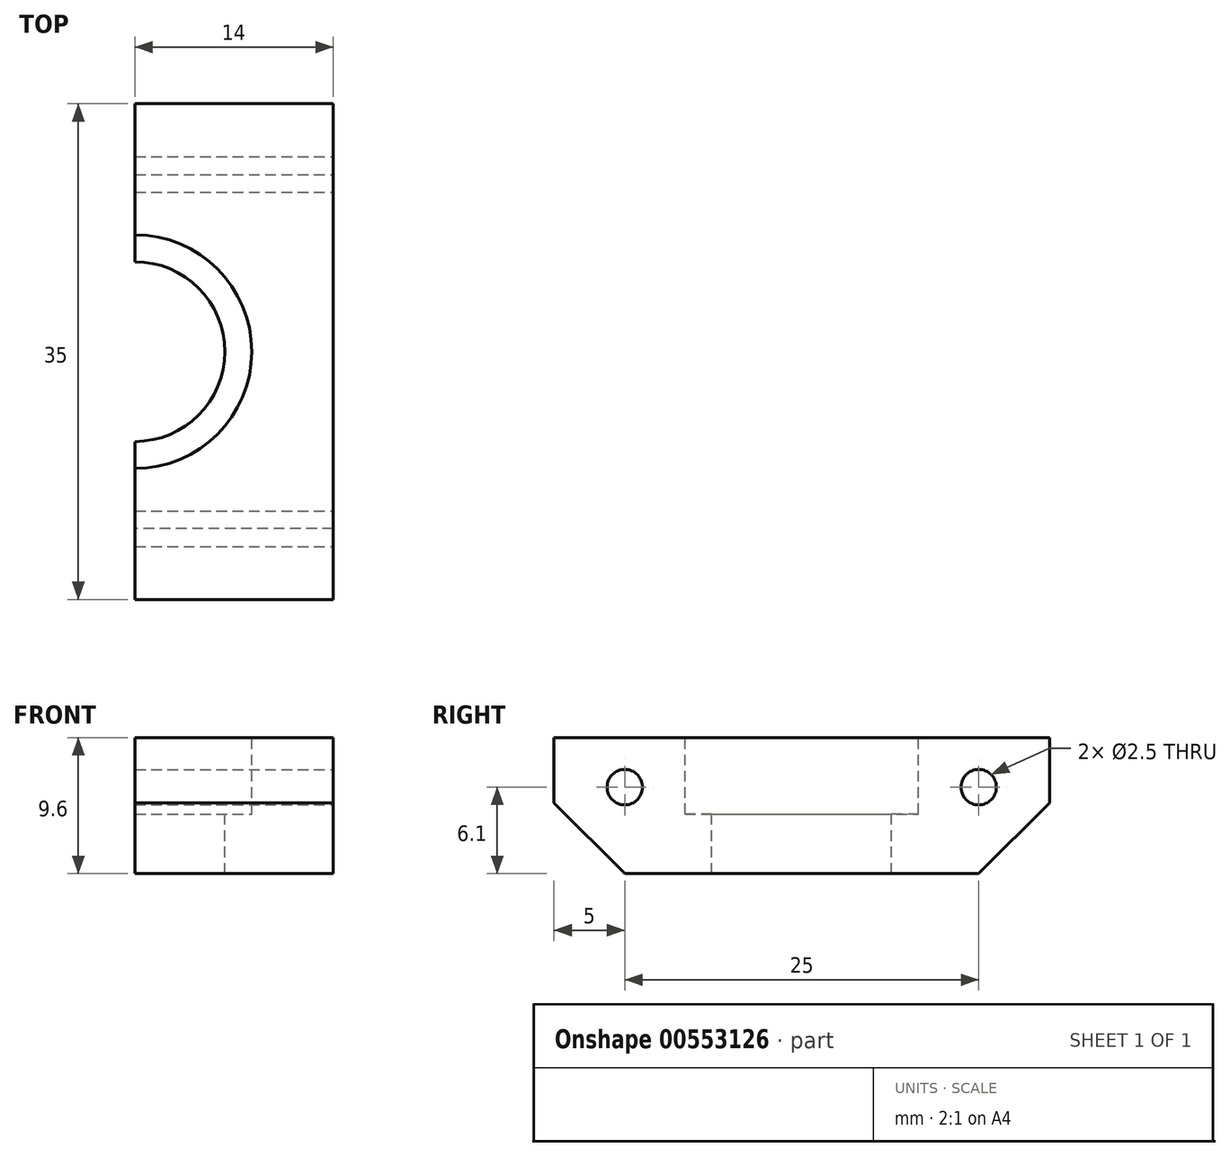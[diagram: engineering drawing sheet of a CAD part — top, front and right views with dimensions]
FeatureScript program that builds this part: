
annotation { "Feature Type Name" : "Feature", "Feature Type Description" : "" }
export const myFeature = defineFeature(function(context is Context, id is Id, definition is map)
    precondition{}
    {
        {
            var Q0;
            Q0=qCreatedBy(makeId("Right.planeOp"),FACE);
            var sketch = newSketch(context, id + "F0", { "sketchPlane" : qUnion([Q0])});
            skLineSegment(sketch, "E0.bottom", {"start": v(-17.5, -4.8) * mm, "end": v(17.5, -4.8) * mm});
            skLineSegment(sketch, "E0.top", {"start": v(-17.5, 4.8) * mm, "end": v(17.5, 4.8) * mm});
            skLineSegment(sketch, "E0.left", {"start": v(-17.5, -4.8) * mm, "end": v(-17.5, 4.8) * mm});
            skLineSegment(sketch, "E0.right", {"start": v(17.5, -4.8) * mm, "end": v(17.5, 4.8) * mm});
            skPoint(sketch, "E0.middle", {"position": v(0, 0) * mm});
            skSolve(sketch);
        }
        {
            var Q0;
            Q0 = qSketchRegion(id + "F0", true);
            extrude(context, id + "F1", {"entities" : qUnion([Q0]), "depth" : 14 * mm, "offsetDistance" : 25 * mm});
        }
        {
            var Q0;
            Q0=makeQuery(id+"F1.opExtrude","SWEPT_FACE",FACE,{"disambiguationData":[OSD([sQuery(id+"F0.wireOp",EDGE,"E0.top")])]});
            var sketch = newSketch(context, id + "F2", { "sketchPlane" : qUnion([Q0])});
            skCircle(sketch, "E1", {"center": v(0, 0) * mm, "radius": 6.35 * mm});
            skCircle(sketch, "E2", {"center": v(0, 0) * mm, "radius": 8.25 * mm});
            skSolve(sketch);
        }
        {
            var Q0;
            Q0 = qSketchRegion(id + "F2", true);
            var Q1;
            {var subQ0=sQuery(id+"F2.wireOp",EDGE,"E1");var subQ1=makeQuery(id+"F1.opExtrude","CAP_EDGE",EDGE,{"disambiguationData":[OSD([sQuery(id+"F0.wireOp",EDGE,"E0.top")])],"isStart":true});var subQ2=makeQuery(id+"F2.imprint","INTERSECT",VERTEX,{"disambiguationData":[OD(0.0)],"derivedFrom":[subQ1,subQ0]});Q1=makeQuery(id+"F2.imprint","IMPRINT",FACE,{"disambiguationData":[TD([[makeQuery(id+"F2.imprint","IMPRINT",EDGE,{"disambiguationData":[TD([[subQ2,1.0]])],"derivedFrom":subQ0}),1.0]])]});}
            var Q2;
            {var subQ0=sQuery(id+"F2.wireOp",EDGE,"E1");var subQ1=makeQuery(id+"F1.opExtrude","CAP_EDGE",EDGE,{"disambiguationData":[OSD([sQuery(id+"F0.wireOp",EDGE,"E0.top")])],"isStart":true});var subQ2=makeQuery(id+"F2.imprint","INTERSECT",VERTEX,{"disambiguationData":[OD(0.0)],"derivedFrom":[subQ1,subQ0]});Q2=makeQuery(id+"F2.imprint","IMPRINT",FACE,{"disambiguationData":[TD([[makeQuery(id+"F2.imprint","IMPRINT",EDGE,{"disambiguationData":[TD([[subQ2,-1.0]])],"derivedFrom":subQ0}),1.0]])]});}
            extrude(context, id + "F3", {"entities" : qUnion([Q0, Q1, Q2]), "operationType" : NewBodyOperationType.REMOVE, "oppositeDirection" : true, "depth" : 5.4 * mm, "offsetDistance" : 25 * mm});
        }
        {
            var Q0;
            {var subQ0=sQuery(id+"F2.wireOp",EDGE,"E1");var subQ1=makeQuery(id+"F1.opExtrude","CAP_EDGE",EDGE,{"disambiguationData":[OSD([sQuery(id+"F0.wireOp",EDGE,"E0.top")])],"isStart":true});var subQ2=makeQuery(id+"F2.imprint","INTERSECT",VERTEX,{"disambiguationData":[OD(0.0)],"derivedFrom":[subQ1,subQ0]});Q0=makeQuery(id+"F2.imprint","IMPRINT",FACE,{"disambiguationData":[TD([[makeQuery(id+"F2.imprint","IMPRINT",EDGE,{"disambiguationData":[TD([[subQ2,-1.0]])],"derivedFrom":subQ0}),1.0]])]});}
            extrude(context, id + "F4", {"entities" : qUnion([Q0]), "operationType" : NewBodyOperationType.REMOVE, "oppositeDirection" : true, "depth" : 25 * mm, "offsetDistance" : 25 * mm});
        }
        {
            var Q0;
            Q0=makeQuery(id+"F1.opExtrude","SWEPT_EDGE",EDGE,{"disambiguationData":[OSD([sQuery(id+"F0.wireOp",EDGE,"E0.bottom"),sQuery(id+"F0.wireOp",EDGE,"E0.right")])]});
            var Q1;
            Q1=makeQuery(id+"F1.opExtrude","SWEPT_EDGE",EDGE,{"disambiguationData":[OSD([sQuery(id+"F0.wireOp",EDGE,"E0.bottom"),sQuery(id+"F0.wireOp",EDGE,"E0.left")])]});
            chamfer(context, id + "F5", {"entities" : qUnion([Q0, Q1]), "width" : 5 * mm, "tangentPropagation" : true});
        }
        {
            var Q0;
            Q0=makeQuery(id+"F1.opExtrude","CAP_FACE",FACE,{"disambiguationData":[OSD([sQuery(id+"F0.wireOp",EDGE,"E0.bottom"),sQuery(id+"F0.wireOp",EDGE,"E0.top"),sQuery(id+"F0.wireOp",EDGE,"E0.left"),sQuery(id+"F0.wireOp",EDGE,"E0.right")])],"isStart":false});
            var sketch = newSketch(context, id + "F6", { "sketchPlane" : qUnion([Q0])});
            skPoint(sketch, "E3", {"position": v(-12.5, 1.3) * mm});
            skPoint(sketch, "E4", {"position": v(12.5, 1.3) * mm});
            skLineSegment(sketch, "E5", {"start": v(-17.5, 1.3) * mm, "end": v(17.5, 1.3) * mm, "construction": true});
            skSolve(sketch);
        }
        {
            var Q0;
            Q0=sQuery(id+"F6.wireOp",VERTEX,"E3");
            var Q1;
            Q1=sQuery(id+"F6.wireOp",VERTEX,"E4");
            var Q2;
            Q2=makeQuery(id+"F1.opExtrude","SWEPT_BODY",BODY,{"disambiguationData":[OSD([sQuery(id+"F0.wireOp",EDGE,"E0.bottom"),sQuery(id+"F0.wireOp",EDGE,"E0.top"),sQuery(id+"F0.wireOp",EDGE,"E0.left"),sQuery(id+"F0.wireOp",EDGE,"E0.right")])]});
            hole(context, id + "F7", {"style" : HoleStyle.SIMPLE, "endStyle" : HoleEndStyle.THROUGH, "holeDiameter" : 2.5 * mm, "majorDiameter" : 5 * mm, "isTappedThrough" : true, "tappedDepth" : 12 * mm, "tapClearance" : 3, "locations" : qUnion([Q0, Q1]), "scope" : qUnion([Q2])});
        }
    });
